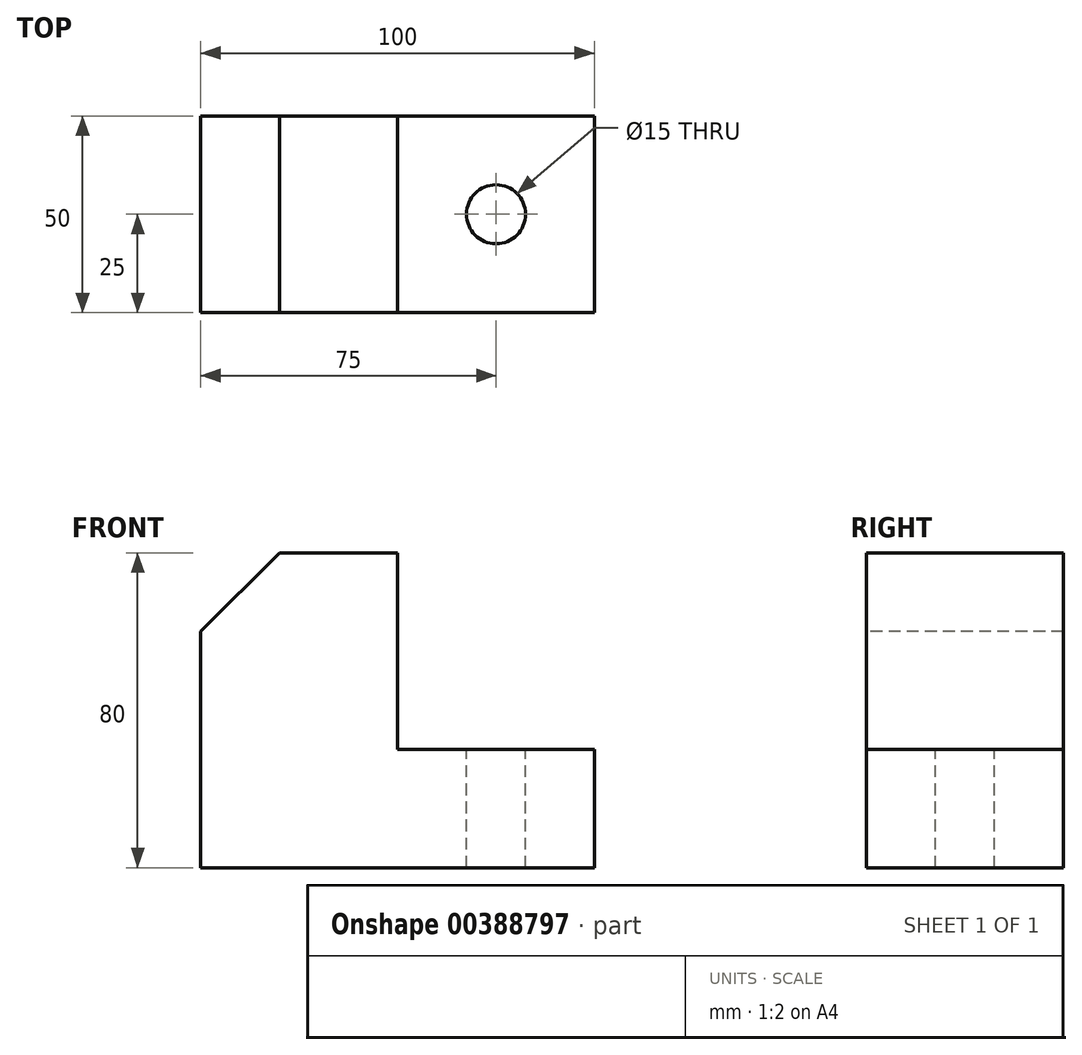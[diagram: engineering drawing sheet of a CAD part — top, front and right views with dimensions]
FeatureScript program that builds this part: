
annotation { "Feature Type Name" : "Feature", "Feature Type Description" : "" }
export const myFeature = defineFeature(function(context is Context, id is Id, definition is map)
    precondition{}
    {
        {
            var Q0;
            Q0=qCreatedBy(makeId("Top.planeOp"),FACE);
            var sketch = newSketch(context, id + "F0", { "sketchPlane" : qUnion([Q0])});
            skLineSegment(sketch, "E0.bottom", {"start": v(0, 0) * mm, "end": v(100, 0) * mm});
            skLineSegment(sketch, "E0.top", {"start": v(0, 50) * mm, "end": v(100, 50) * mm});
            skLineSegment(sketch, "E0.left", {"start": v(0, 0) * mm, "end": v(0, 50) * mm});
            skLineSegment(sketch, "E0.right", {"start": v(100, 0) * mm, "end": v(100, 50) * mm});
            skSolve(sketch);
        }
        {
            var Q0;
            Q0 = qSketchRegion(id + "F0", true);
            extrude(context, id + "F1", {"entities" : qUnion([Q0]), "depth" : 30 * mm});
        }
        {
            var Q0;
            Q0=makeQuery(id+"F1.opExtrude","CAP_FACE",FACE,{"disambiguationData":[OSD([sQuery(id+"F0.wireOp",EDGE,"E0.bottom"),sQuery(id+"F0.wireOp",EDGE,"E0.top"),sQuery(id+"F0.wireOp",EDGE,"E0.left"),sQuery(id+"F0.wireOp",EDGE,"E0.right")])],"isStart":true});
            cPlane(context, id + "F2", {"entities" : qUnion([Q0]), "cplaneType" : CPlaneType.OFFSET, "offset" : 80 * mm, "oppositeDirection" : true, "width" : 150 * mm, "height" : 150 * mm});
        }
        {
            var Q0;
            Q0=makeQuery(id+"F1.opExtrude","CAP_FACE",FACE,{"disambiguationData":[OSD([sQuery(id+"F0.wireOp",EDGE,"E0.bottom"),sQuery(id+"F0.wireOp",EDGE,"E0.top"),sQuery(id+"F0.wireOp",EDGE,"E0.left"),sQuery(id+"F0.wireOp",EDGE,"E0.right")])],"isStart":false});
            var sketch = newSketch(context, id + "F3", { "sketchPlane" : qUnion([Q0])});
            skLineSegment(sketch, "E1.bottom", {"start": v(0, 0) * mm, "end": v(50, 0) * mm});
            skLineSegment(sketch, "E1.top", {"start": v(0, 50) * mm, "end": v(50, 50) * mm});
            skLineSegment(sketch, "E1.left", {"start": v(0, 0) * mm, "end": v(0, 50) * mm});
            skLineSegment(sketch, "E1.right", {"start": v(50, 0) * mm, "end": v(50, 50) * mm});
            skSolve(sketch);
        }
        {
            var Q0;
            Q0 = qSketchRegion(id + "F3", true);
            var Q1;
            Q1=qCreatedBy(id+"F2.planeOp",FACE);
            extrude(context, id + "F4", {"entities" : qUnion([Q0]), "operationType" : NewBodyOperationType.ADD, "endBound" : BoundingType.UP_TO_SURFACE, "endBoundEntityFace" : qUnion([Q1]), "depth" : 25 * mm});
        }
        {
            var Q0;
            Q0=makeQuery(id+"F4.boolean.opBoolean","MERGE",FACE,{"derivedFrom":[makeQuery(id+"F1.opExtrude","SWEPT_FACE",FACE,{"disambiguationData":[OSD([sQuery(id+"F0.wireOp",EDGE,"E0.bottom")])]}),makeQuery(id+"F4.opExtrude","SWEPT_FACE",FACE,{"disambiguationData":[OSD([sQuery(id+"F3.wireOp",EDGE,"E1.bottom")])]})]});
            var sketch = newSketch(context, id + "F5", { "sketchPlane" : qUnion([Q0])});
            skLineSegment(sketch, "E2", {"start": v(0, 80) * mm, "end": v(20, 80) * mm});
            skLineSegment(sketch, "E3", {"start": v(20, 80) * mm, "end": v(0, 60) * mm});
            skLineSegment(sketch, "E4", {"start": v(0, 60) * mm, "end": v(0, 80) * mm});
            skSolve(sketch);
        }
        {
            var Q0;
            Q0 = qSketchRegion(id + "F5", true);
            extrude(context, id + "F6", {"entities" : qUnion([Q0]), "operationType" : NewBodyOperationType.REMOVE, "endBound" : BoundingType.UP_TO_NEXT, "oppositeDirection" : true, "depth" : 25 * mm});
        }
        {
            var Q0;
            Q0=makeQuery(id+"F1.opExtrude","CAP_FACE",FACE,{"disambiguationData":[OSD([sQuery(id+"F0.wireOp",EDGE,"E0.bottom"),sQuery(id+"F0.wireOp",EDGE,"E0.top"),sQuery(id+"F0.wireOp",EDGE,"E0.left"),sQuery(id+"F0.wireOp",EDGE,"E0.right")])],"isStart":false});
            var sketch = newSketch(context, id + "F7", { "sketchPlane" : qUnion([Q0])});
            skCircle(sketch, "E5", {"center": v(75, 25) * mm, "radius": 7.5 * mm});
            skSolve(sketch);
        }
        {
            var Q0;
            Q0=makeQuery(id+"F7.imprint","IMPRINT",FACE,{"disambiguationData":[TD([[makeQuery(id+"F7.imprint","IMPRINT",EDGE,{"derivedFrom":sQuery(id+"F7.wireOp",EDGE,"E5")}),1.0]])]});
            extrude(context, id + "F8", {"entities" : qUnion([Q0]), "operationType" : NewBodyOperationType.REMOVE, "endBound" : BoundingType.THROUGH_ALL, "oppositeDirection" : true, "depth" : 25 * mm});
        }
    });
